# Revit family: Vitra-ShowerCornerBasket-ArkitektaSeries-A44380
name_source: partatom
category: Plumbing Fixtures
revit_build: Autodesk Revit 2017 (Build: 20160225_1515(x64)
units: mm (PartAtom-declared; Revit-internal decimal feet)

## family parameters
Cut with Voids When Loaded = No
Host = Face
OmniClass Number = 23.45.55.17
OmniClass Title = Mixing Faucets
Part Type = Normal
Room Calculation Point = No
Round Connector Dimension = Use Diameter
Shared = Yes

## types (2) — shared parameters
BIMobject category = Shower trays
CW Connection = No
Default Elevation = 2200 mm
Depth(mm) = 200 mm  [stored 0.656168 ft]
Design country = Turkey
HW Connection = No
Height(mm) = 55 mm  [stored 0.180446 ft]
IFC Classification = Sanitary Terminal
Manufacturer = Vitra
Manufacturer name = Vitra
Masterformat 2014 Code = 01 52 19
Masterformat 2014 Description = Sanitary Facilities
MountingType = Wall-mounted
NBS Referans Code = 31-75
NBS Referans Description = Sanitary Accessories
Nominal height = 0.000
Nominal width = 0.000
OmniClass Code = 23-19 31 17
OmniClass Description = Sanitary Room Units
Product Type = Built-in Shower Corner Basket
Product certification = https://vitraglobal.com
Product data url = https://www.vitra.com.tr
Product family = ArkitektaSeries
Product group = Shower Corner Basket
Technical description = https://www.vitra.com.tr
UNSPSC Code = 301815
URL = https://vitraglobal.com
Uniclass 1.4 Code = L721
Uniclass 1.4 Description = Sanitary equipment
Uniclass 2.0 Code = PR-31-75
Uniclass 2.0 Description = Sanitary Accessories
Uniclass 2015 Code = Pr_40_20
Uniclass 2015 Name = Sanitary fittings and accessories
Uniformat II Code = E1090
Uniformat II Description = Other Equipment
Weight Net (kg) = 0,495
Width(mm) = 200 mm  [stored 0.656168 ft]
Youtube = https://www.youtube.com
zero-valued in all types: CWFU, Cost, HWFU, WFU

## per-type parameters (varying)
| type | Article No. (default) | Coating Material | Color | Model | Product SKU |
| ShowerCornerBasket-Vitra-ArkitektaSeries-A44380 | A44380 | Vitra-Chrome | Chrome | A44380 | A44380 |
| ShowerCornerBasket-Vitra-ArkitektaSeries-A4438023 | A4438023 | Vitra-Gold | Gold | A4438023 | A4438023 |

note: [stored X ft] marks values corroborated as IEEE doubles in the binary element streams (Revit-internal decimal feet)

## geometry (parser evidence)
native form markers: Sweep x3
no freeform markers — native parametric forms only
